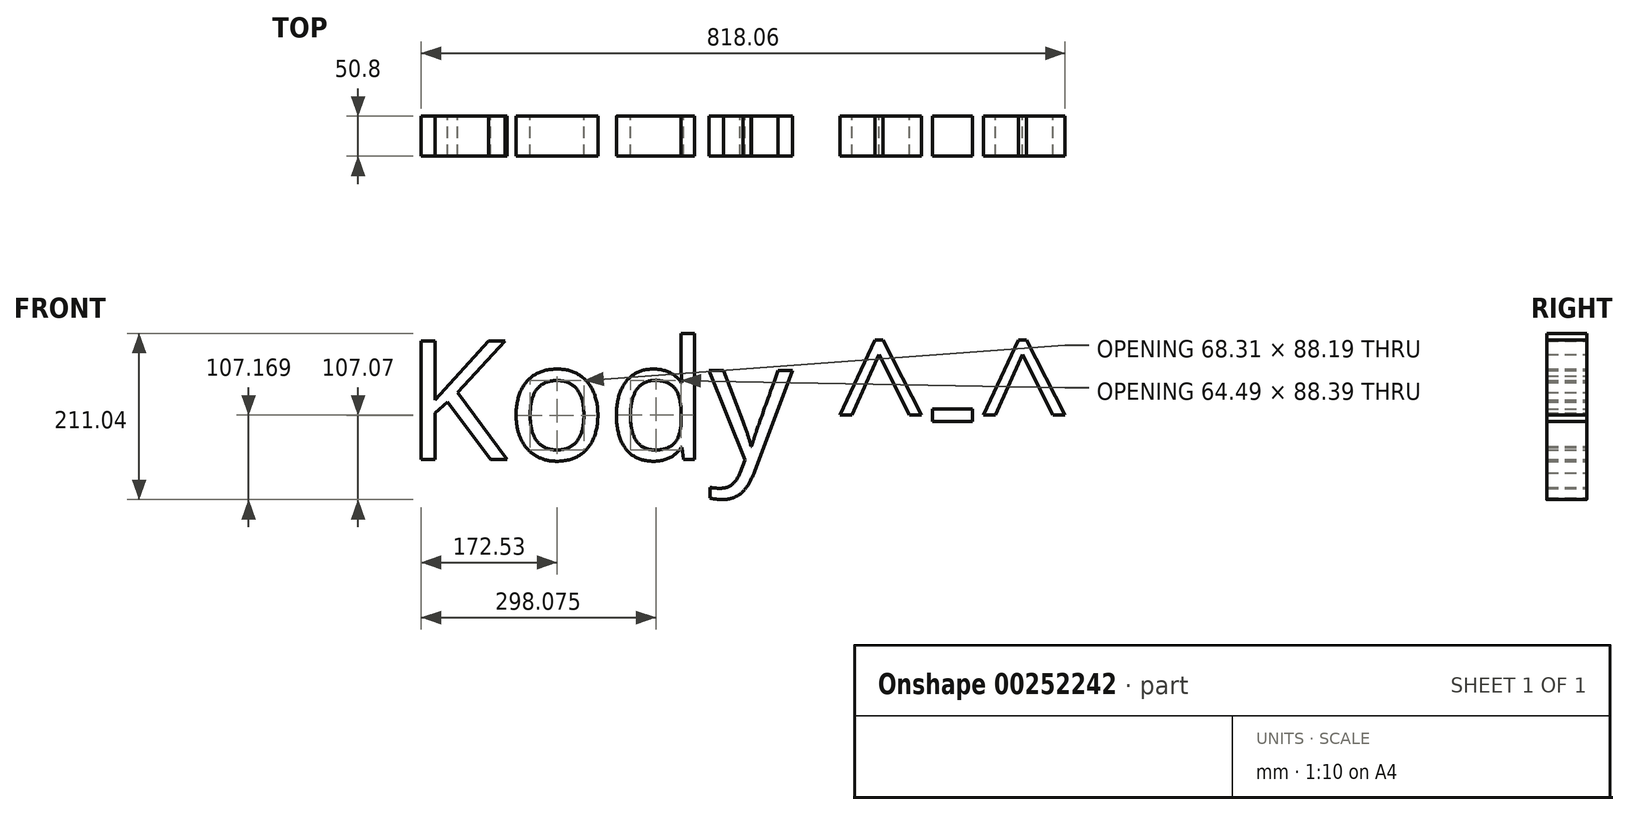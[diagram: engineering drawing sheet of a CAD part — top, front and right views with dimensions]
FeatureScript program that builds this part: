
annotation { "Feature Type Name" : "Feature", "Feature Type Description" : "" }
export const myFeature = defineFeature(function(context is Context, id is Id, definition is map)
    precondition{}
    {
        {
            var Q0;
            Q0=qCreatedBy(makeId("Front.planeOp"),FACE);
            var sketch = newSketch(context, id + "F0", { "sketchPlane" : qUnion([Q0])});
            skText(sketch, "E0", { "text": "Kody ^-^", "fontName": "OpenSans-Regular.ttf"});
            const initialGuessF0  = {"E0": [-0.07625, -0.07596, 1, 0, 0.15192]};
            skSetInitialGuess(sketch, initialGuessF0);
            skSolve(sketch);
        }
        {
            var Q0;
            Q0 = qSketchRegion(id + "F0", true);
            extrude(context, id + "F1", {"entities" : qUnion([Q0]), "depth" : 50.8 * mm});
        }
    });
